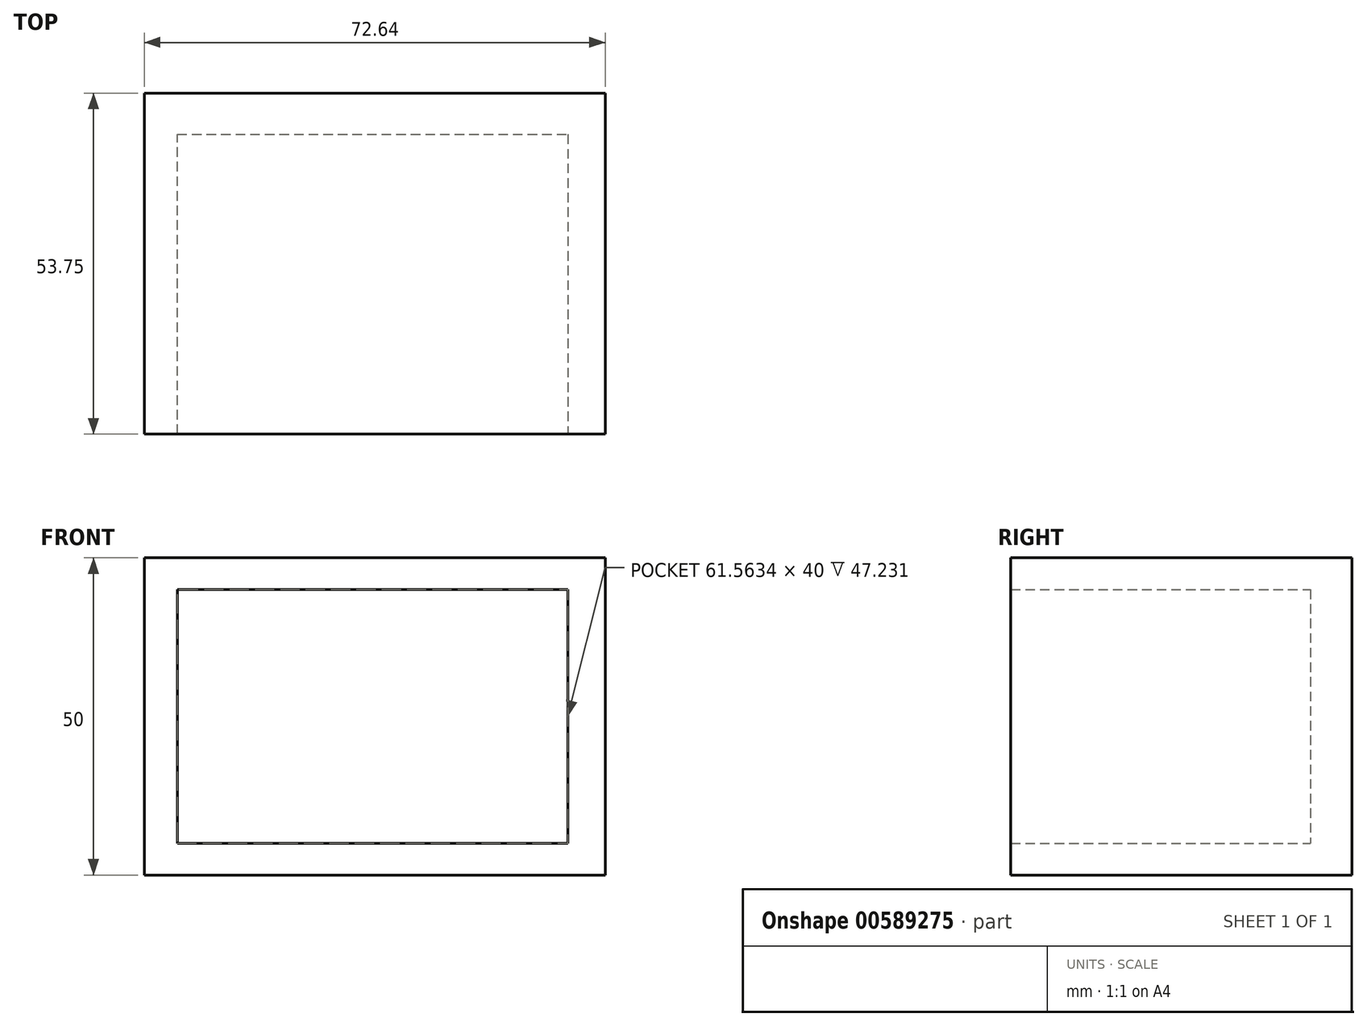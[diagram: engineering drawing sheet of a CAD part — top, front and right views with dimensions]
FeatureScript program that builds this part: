
annotation { "Feature Type Name" : "Feature", "Feature Type Description" : "" }
export const myFeature = defineFeature(function(context is Context, id is Id, definition is map)
    precondition{}
    {
        {
            var Q0;
            Q0=qCreatedBy(makeId("Top.planeOp"),FACE);
            var sketch = newSketch(context, id + "F0", { "sketchPlane" : qUnion([Q0])});
            skLineSegment(sketch, "E0", {"start": v(-34.04, -16.94) * mm, "end": v(-34.04, 30.3) * mm});
            skLineSegment(sketch, "E1", {"start": v(-34.04, 30.3) * mm, "end": v(27.52, 30.3) * mm});
            skLineSegment(sketch, "E2", {"start": v(27.52, 30.3) * mm, "end": v(27.52, -16.94) * mm});
            skLineSegment(sketch, "E3", {"start": v(27.52, -16.94) * mm, "end": v(33.39, -16.94) * mm});
            skLineSegment(sketch, "E4", {"start": v(33.39, -16.94) * mm, "end": v(33.39, 36.8) * mm});
            skLineSegment(sketch, "E5", {"start": v(33.39, 36.8) * mm, "end": v(-39.25, 36.8) * mm});
            skLineSegment(sketch, "E6", {"start": v(-39.25, 36.8) * mm, "end": v(-39.25, -16.94) * mm});
            skLineSegment(sketch, "E7", {"start": v(-39.25, -16.94) * mm, "end": v(-34.04, -16.94) * mm});
            skSolve(sketch);
        }
        {
            var Q0;
            Q0 = qSketchRegion(id + "F0", true);
            extrude(context, id + "F1", {"entities" : qUnion([Q0]), "depth" : 50 * mm, "offsetDistance" : 25 * mm});
        }
        {
            var Q0;
            Q0=qCreatedBy(makeId("Top.planeOp"),FACE);
            cPlane(context, id + "F2", {"entities" : qUnion([Q0]), "cplaneType" : CPlaneType.OFFSET, "offset" : 50 * mm, "width" : 150 * mm, "height" : 150 * mm});
        }
        {
            var Q0;
            Q0=qCreatedBy(id+"F2.planeOp",FACE);
            var sketch = newSketch(context, id + "F3", { "sketchPlane" : qUnion([Q0])});
            skLineSegment(sketch, "E8", {"start": v(33.39, 36.8) * mm, "end": v(-39.25, 36.8) * mm});
            skLineSegment(sketch, "E9", {"start": v(-39.25, 36.8) * mm, "end": v(-39.25, -16.94) * mm});
            skLineSegment(sketch, "E10", {"start": v(-39.25, -16.94) * mm, "end": v(33.39, -16.94) * mm});
            skLineSegment(sketch, "E11", {"start": v(33.39, -16.94) * mm, "end": v(33.39, 36.8) * mm});
            skSolve(sketch);
        }
        {
            var Q0;
            Q0 = qSketchRegion(id + "F3", true);
            extrude(context, id + "F4", {"entities" : qUnion([Q0]), "operationType" : NewBodyOperationType.ADD, "oppositeDirection" : true, "depth" : 5 * mm, "offsetDistance" : 25 * mm});
        }
        {
            var Q0;
            Q0=qCreatedBy(makeId("Top.planeOp"),FACE);
            var sketch = newSketch(context, id + "F5", { "sketchPlane" : qUnion([Q0])});
            skLineSegment(sketch, "E12", {"start": v(-39.25, 36.8) * mm, "end": v(33.39, 36.8) * mm});
            skLineSegment(sketch, "E13", {"start": v(-39.25, 36.8) * mm, "end": v(-39.25, -16.94) * mm});
            skLineSegment(sketch, "E14", {"start": v(-39.25, -16.94) * mm, "end": v(33.39, -16.94) * mm});
            skLineSegment(sketch, "E15", {"start": v(33.39, -16.94) * mm, "end": v(33.39, 36.8) * mm});
            skSolve(sketch);
        }
        {
            var Q0;
            Q0 = qSketchRegion(id + "F5", true);
            extrude(context, id + "F6", {"entities" : qUnion([Q0]), "operationType" : NewBodyOperationType.ADD, "depth" : 5 * mm, "offsetDistance" : 25 * mm});
        }
    });
